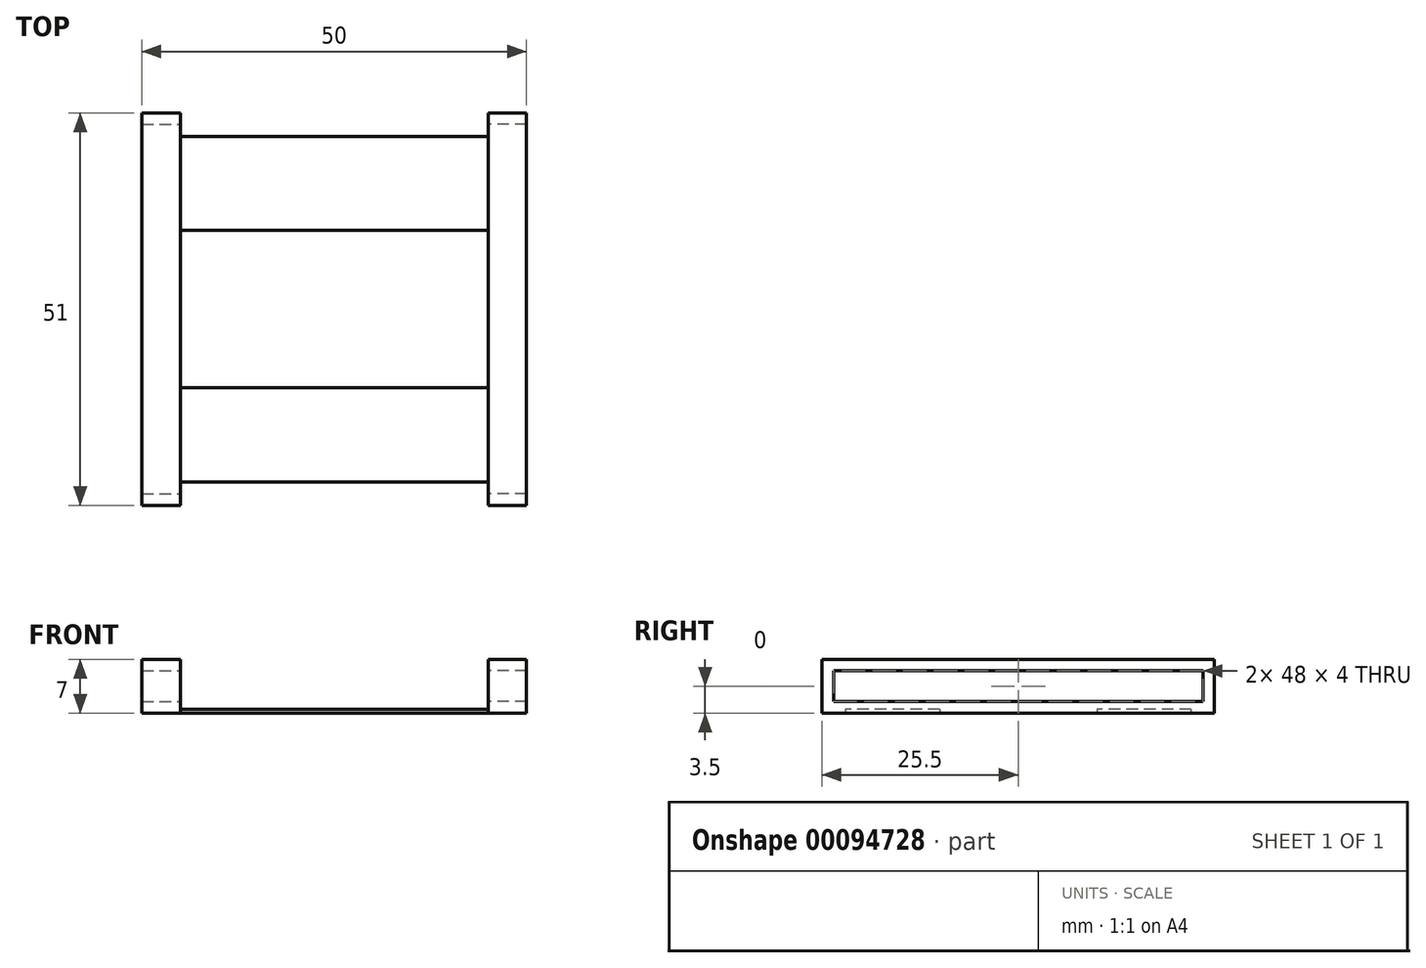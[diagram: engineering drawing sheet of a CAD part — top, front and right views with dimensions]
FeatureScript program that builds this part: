
annotation { "Feature Type Name" : "Feature", "Feature Type Description" : "" }
export const myFeature = defineFeature(function(context is Context, id is Id, definition is map)
    precondition{}
    {
        {
            var Q0;
            Q0=qCreatedBy(makeId("Right.planeOp"),FACE);
            var sketch = newSketch(context, id + "F0", { "sketchPlane" : qUnion([Q0])});
            skLineSegment(sketch, "E0.bottom", {"start": v(-25.5, 0) * mm, "end": v(25.5, 0) * mm});
            skLineSegment(sketch, "E0.top", {"start": v(-25.5, 7) * mm, "end": v(25.5, 7) * mm});
            skLineSegment(sketch, "E0.left", {"start": v(-25.5, 0) * mm, "end": v(-25.5, 7) * mm});
            skLineSegment(sketch, "E0.right", {"start": v(25.5, 0) * mm, "end": v(25.5, 7) * mm});
            skPoint(sketch, "E0.middle", {"position": v(0, 3.5) * mm});
            skLineSegment(sketch, "E1.bottom", {"start": v(-24, 1.5) * mm, "end": v(24, 1.5) * mm});
            skLineSegment(sketch, "E1.top", {"start": v(-24, 5.5) * mm, "end": v(24, 5.5) * mm});
            skLineSegment(sketch, "E1.left", {"start": v(-24, 1.5) * mm, "end": v(-24, 5.5) * mm});
            skLineSegment(sketch, "E1.right", {"start": v(24, 1.5) * mm, "end": v(24, 5.5) * mm});
            skLineSegment(sketch, "E2.bottom", {"start": v(-22.46, 0) * mm, "end": v(-10.22, 0) * mm});
            skLineSegment(sketch, "E2.top", {"start": v(-22.46, 0.5) * mm, "end": v(-10.22, 0.5) * mm});
            skLineSegment(sketch, "E2.left", {"start": v(-22.46, 0) * mm, "end": v(-22.46, 0.5) * mm});
            skLineSegment(sketch, "E2.right", {"start": v(-10.22, 0) * mm, "end": v(-10.22, 0.5) * mm});
            skLineSegment(sketch, "E3.bottom", {"start": v(10.22, 0) * mm, "end": v(22.46, 0) * mm});
            skLineSegment(sketch, "E3.top", {"start": v(10.22, 0.5) * mm, "end": v(22.46, 0.5) * mm});
            skLineSegment(sketch, "E3.left", {"start": v(10.22, 0) * mm, "end": v(10.22, 0.5) * mm});
            skLineSegment(sketch, "E3.right", {"start": v(22.46, 0) * mm, "end": v(22.46, 0.5) * mm});
            skSolve(sketch);
        }
        {
            var Q0;
            Q0=makeQuery(id+"F0.imprint","IMPRINT",FACE,{"disambiguationData":[TD([[makeQuery(id+"F0.imprint","IMPRINT",EDGE,{"derivedFrom":sQuery(id+"F0.wireOp",EDGE,"E0.top")}),-1.0]])]});
            var Q1;
            Q1=makeQuery(id+"F0.imprint","IMPRINT",FACE,{"disambiguationData":[TD([[makeQuery(id+"F0.imprint","IMPRINT",EDGE,{"derivedFrom":sQuery(id+"F0.wireOp",EDGE,"E2.top")}),-1.0]])]});
            var Q2;
            Q2=makeQuery(id+"F0.imprint","IMPRINT",FACE,{"disambiguationData":[TD([[makeQuery(id+"F0.imprint","IMPRINT",EDGE,{"derivedFrom":sQuery(id+"F0.wireOp",EDGE,"E3.top")}),-1.0]])]});
            extrude(context, id + "F1", {"entities" : qUnion([Q0, Q1, Q2]), "depth" : 25 * mm, "offsetDistance" : 25 * mm, "hasSecondDirection" : true, "secondDirectionOppositeDirection" : false, "secondDirectionDepth" : 20 * mm});
        }
        {
            var Q0;
            Q0=makeQuery(id+"F0.imprint","IMPRINT",FACE,{"disambiguationData":[TD([[makeQuery(id+"F0.imprint","IMPRINT",EDGE,{"derivedFrom":sQuery(id+"F0.wireOp",EDGE,"E0.top")}),-1.0]])]});
            var Q1;
            Q1=makeQuery(id+"F0.imprint","IMPRINT",FACE,{"disambiguationData":[TD([[makeQuery(id+"F0.imprint","IMPRINT",EDGE,{"derivedFrom":sQuery(id+"F0.wireOp",EDGE,"E2.top")}),-1.0]])]});
            var Q2;
            Q2=makeQuery(id+"F0.imprint","IMPRINT",FACE,{"disambiguationData":[TD([[makeQuery(id+"F0.imprint","IMPRINT",EDGE,{"derivedFrom":sQuery(id+"F0.wireOp",EDGE,"E3.top")}),-1.0]])]});
            extrude(context, id + "F2", {"entities" : qUnion([Q0, Q1, Q2]), "oppositeDirection" : true, "depth" : 25 * mm, "offsetDistance" : 25 * mm, "hasSecondDirection" : true, "secondDirectionOppositeDirection" : true, "secondDirectionDepth" : 20 * mm});
        }
        {
            var Q0;
            Q0=makeQuery(id+"F0.imprint","IMPRINT",FACE,{"disambiguationData":[TD([[makeQuery(id+"F0.imprint","IMPRINT",EDGE,{"derivedFrom":sQuery(id+"F0.wireOp",EDGE,"E3.top")}),-1.0]])]});
            var Q1;
            Q1=makeQuery(id+"F0.imprint","IMPRINT",FACE,{"disambiguationData":[TD([[makeQuery(id+"F0.imprint","IMPRINT",EDGE,{"derivedFrom":sQuery(id+"F0.wireOp",EDGE,"E2.top")}),-1.0]])]});
            extrude(context, id + "F3", {"entities" : qUnion([Q0, Q1]), "operationType" : NewBodyOperationType.ADD, "depth" : 25 * mm, "offsetDistance" : 25 * mm, "hasSecondDirection" : true, "secondDirectionOppositeDirection" : true, "secondDirectionDepth" : 25 * mm});
        }
    });
